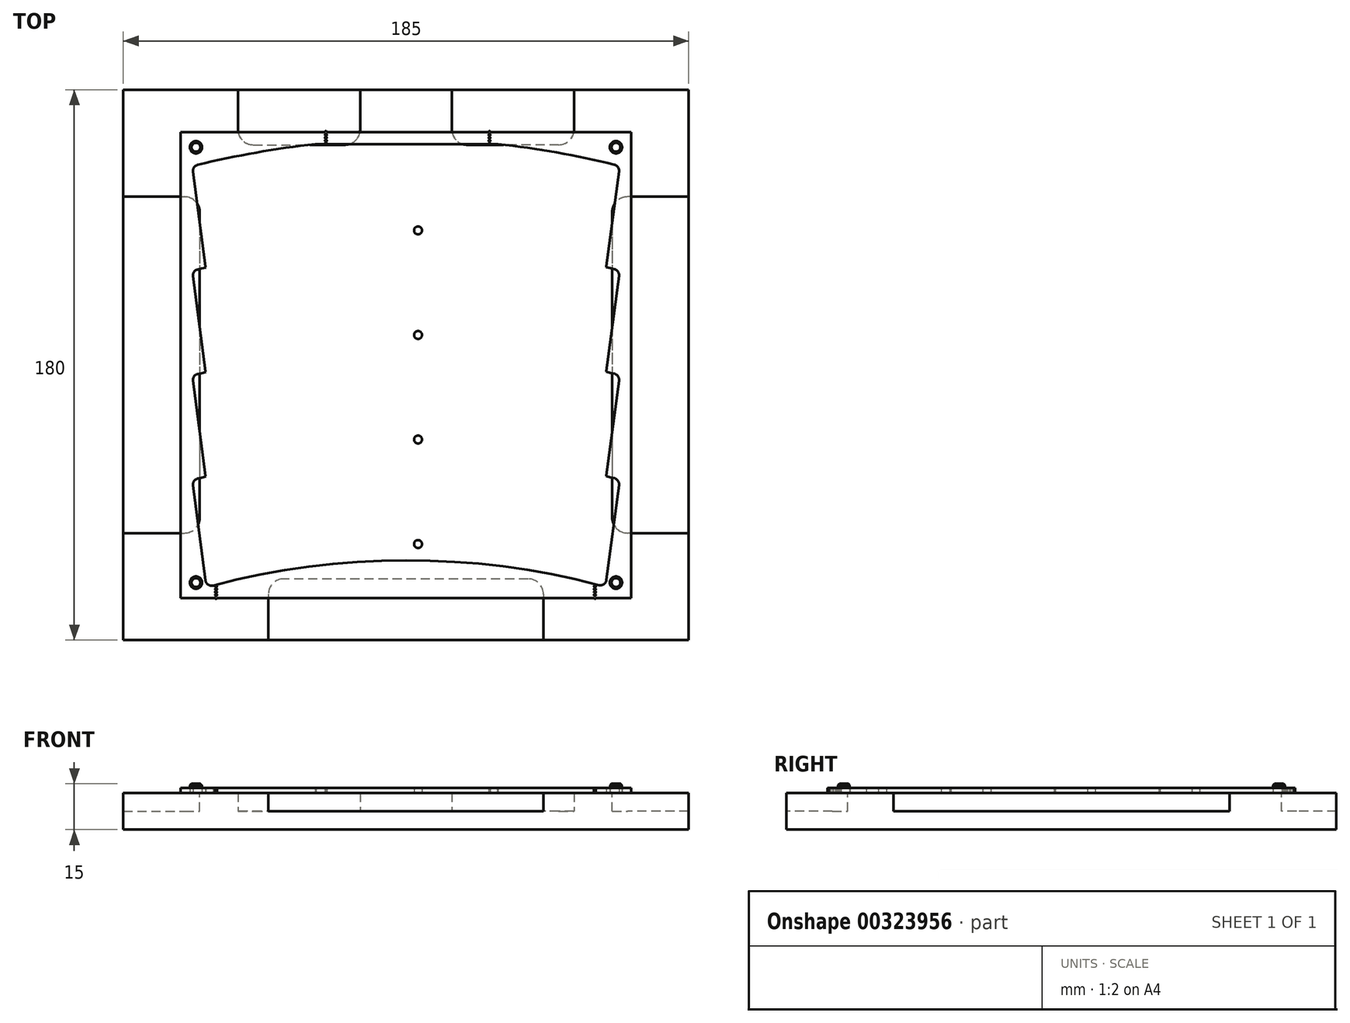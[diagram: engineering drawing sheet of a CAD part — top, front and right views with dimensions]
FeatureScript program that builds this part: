
annotation { "Feature Type Name" : "Feature", "Feature Type Description" : "" }
export const myFeature = defineFeature(function(context is Context, id is Id, definition is map)
    precondition{}
    {
        {
            var Q0;
            Q0=qCreatedBy(makeId("Top.planeOp"),FACE);
            var sketch = newSketch(context, id + "F0", { "sketchPlane" : qUnion([Q0])});
            skLineSegment(sketch, "E0.bottom", {"start": v(92.5, 90) * mm, "end": v(-92.5, 90) * mm});
            skLineSegment(sketch, "E0.top", {"start": v(92.5, -90) * mm, "end": v(-92.5, -90) * mm});
            skLineSegment(sketch, "E0.left", {"start": v(92.5, 90) * mm, "end": v(92.5, -90) * mm});
            skLineSegment(sketch, "E0.right", {"start": v(-92.5, 90) * mm, "end": v(-92.5, -90) * mm});
            skPoint(sketch, "E0.middle", {"position": v(0, 0) * mm});
            skSolve(sketch);
        }
        {
            var Q0;
            Q0 = qSketchRegion(id + "F0", true);
            extrude(context, id + "F1", {"entities" : qUnion([Q0]), "depth" : 12 * mm});
        }
        {
            var Q0;
            Q0=makeQuery(id+"F1.opExtrude","CAP_FACE",FACE,{"disambiguationData":[OSD([sQuery(id+"F0.wireOp",EDGE,"E0.bottom"),sQuery(id+"F0.wireOp",EDGE,"E0.top"),sQuery(id+"F0.wireOp",EDGE,"E0.left"),sQuery(id+"F0.wireOp",EDGE,"E0.right")])],"isStart":false});
            var sketch = newSketch(context, id + "F2", { "sketchPlane" : qUnion([Q0])});
            skLineSegment(sketch, "E1.bottom", {"start": v(117.5, 55) * mm, "end": v(72.5, 55) * mm});
            skLineSegment(sketch, "E1.top", {"start": v(117.5, -55) * mm, "end": v(72.5, -55) * mm});
            skLineSegment(sketch, "E1.left", {"start": v(117.5, 55) * mm, "end": v(117.5, -55) * mm});
            skLineSegment(sketch, "E1.right", {"start": v(67.5, 50) * mm, "end": v(67.5, -50) * mm});
            skPoint(sketch, "E1.middle", {"position": v(92.5, 0) * mm});
            skLineSegment(sketch, "E2.bottom", {"start": v(40, -70) * mm, "end": v(-40, -70) * mm});
            skLineSegment(sketch, "E2.top", {"start": v(45, -110) * mm, "end": v(-45, -110) * mm});
            skLineSegment(sketch, "E2.left", {"start": v(45, -75) * mm, "end": v(45, -110) * mm});
            skLineSegment(sketch, "E2.right", {"start": v(-45, -75) * mm, "end": v(-45, -110) * mm});
            skPoint(sketch, "E2.middle", {"position": v(0, -90) * mm});
            skLineSegment(sketch, "E3.bottom", {"start": v(55, 108) * mm, "end": v(15, 108) * mm});
            skLineSegment(sketch, "E3.top", {"start": v(50, 72) * mm, "end": v(20, 72) * mm});
            skLineSegment(sketch, "E3.left", {"start": v(55, 108) * mm, "end": v(55, 77) * mm});
            skLineSegment(sketch, "E3.right", {"start": v(15, 108) * mm, "end": v(15, 77) * mm});
            skPoint(sketch, "E3.middle", {"position": v(35, 90) * mm});
            skLineSegment(sketch, "E4", {"start": v(0, 90) * mm, "end": v(0, 132.09) * mm});
            skPoint(sketch, "E4.endSnap0", {"position": v(0, 90) * mm});
            skLineSegment(sketch, "E5.MirrorCS", {"start": v(-55, 108) * mm, "end": v(-15, 108) * mm});
            skLineSegment(sketch, "E6.MirrorCS", {"start": v(-50, 72) * mm, "end": v(-20, 72) * mm});
            skLineSegment(sketch, "E7.MirrorCS", {"start": v(-15, 108) * mm, "end": v(-15, 77) * mm});
            skLineSegment(sketch, "E8.MirrorCS", {"start": v(-55, 108) * mm, "end": v(-55, 77) * mm});
            skPoint(sketch, "E9.MirrorP", {"position": v(-35, 90) * mm});
            skPoint(sketch, "E10.visualSharp", {"position": v(55, 72) * mm});
            skArc(sketch, "E10.filletArc", {"start": v(50, 72) * mm, "mid": v(53.54, 73.46) * mm, "end": v(55, 77) * mm});
            skPoint(sketch, "E11.visualSharp", {"position": v(15, 72) * mm});
            skArc(sketch, "E11.filletArc", {"start": v(15, 77) * mm, "mid": v(16.46, 73.46) * mm, "end": v(20, 72) * mm});
            skPoint(sketch, "E12.visualSharp", {"position": v(-15, 72) * mm});
            skArc(sketch, "E12.filletArc", {"start": v(-20, 72) * mm, "mid": v(-16.46, 73.46) * mm, "end": v(-15, 77) * mm});
            skPoint(sketch, "E13.visualSharp", {"position": v(-55, 72) * mm});
            skArc(sketch, "E13.filletArc", {"start": v(-55, 77) * mm, "mid": v(-53.54, 73.46) * mm, "end": v(-50, 72) * mm});
            skPoint(sketch, "E14.visualSharp", {"position": v(67.5, 55) * mm});
            skArc(sketch, "E14.filletArc", {"start": v(72.5, 55) * mm, "mid": v(68.96, 53.54) * mm, "end": v(67.5, 50) * mm});
            skPoint(sketch, "E15.visualSharp", {"position": v(67.5, -55) * mm});
            skArc(sketch, "E15.filletArc", {"start": v(67.5, -50) * mm, "mid": v(68.96, -53.54) * mm, "end": v(72.5, -55) * mm});
            skPoint(sketch, "E16.visualSharp", {"position": v(45, -70) * mm});
            skArc(sketch, "E16.filletArc", {"start": v(45, -75) * mm, "mid": v(43.54, -71.46) * mm, "end": v(40, -70) * mm});
            skPoint(sketch, "E17.visualSharp", {"position": v(-45, -70) * mm});
            skArc(sketch, "E17.filletArc", {"start": v(-40, -70) * mm, "mid": v(-43.54, -71.46) * mm, "end": v(-45, -75) * mm});
            skArc(sketch, "E18.MirrorCS", {"start": v(-72.5, 55) * mm, "mid": v(-68.96, 53.54) * mm, "end": v(-67.5, 50) * mm});
            skArc(sketch, "E19.MirrorCS", {"start": v(-67.5, -50) * mm, "mid": v(-68.96, -53.54) * mm, "end": v(-72.5, -55) * mm});
            skPoint(sketch, "E20.MirrorP", {"position": v(-92.5, 0) * mm});
            skLineSegment(sketch, "E21.MirrorCS", {"start": v(-117.5, 55) * mm, "end": v(-72.5, 55) * mm});
            skLineSegment(sketch, "E22.MirrorCS", {"start": v(-117.5, -55) * mm, "end": v(-72.5, -55) * mm});
            skLineSegment(sketch, "E23.MirrorCS", {"start": v(-67.5, 50) * mm, "end": v(-67.5, -50) * mm});
            skLineSegment(sketch, "E24.MirrorCS", {"start": v(-117.5, 55) * mm, "end": v(-117.5, -55) * mm});
            skPoint(sketch, "E25.MirrorP", {"position": v(-67.5, 55) * mm});
            skPoint(sketch, "E26.MirrorP", {"position": v(-67.5, -55) * mm});
            skSolve(sketch);
        }
        {
            var Q0;
            Q0 = qSketchRegion(id + "F2", true);
            extrude(context, id + "F3", {"entities" : qUnion([Q0]), "operationType" : NewBodyOperationType.REMOVE, "oppositeDirection" : true, "depth" : 6 * mm});
        }
        {
            var Q0;
            Q0=makeQuery(id+"F1.opExtrude","CAP_FACE",FACE,{"disambiguationData":[OSD([sQuery(id+"F0.wireOp",EDGE,"E0.bottom"),sQuery(id+"F0.wireOp",EDGE,"E0.top"),sQuery(id+"F0.wireOp",EDGE,"E0.left"),sQuery(id+"F0.wireOp",EDGE,"E0.right")])],"isStart":false});
            var sketch = newSketch(context, id + "F4", { "sketchPlane" : qUnion([Q0])});
            skCircle(sketch, "E27", {"center": v(-65.48, -53.9) * mm, "radius": 0.3 * mm});
            skCircle(sketch, "E28", {"center": v(-65.36, -54.83) * mm, "radius": 0.3 * mm});
            skCircle(sketch, "E29", {"center": v(-65.23, -55.78) * mm, "radius": 0.3 * mm});
            skCircle(sketch, "E30", {"center": v(-65.6, -52.95) * mm, "radius": 0.3 * mm});
            skCircle(sketch, "E31", {"center": v(-65.1, -56.72) * mm, "radius": 0.3 * mm});
            skCircle(sketch, "E32", {"center": v(-65.73, -52) * mm, "radius": 0.3 * mm});
            skCircle(sketch, "E33", {"center": v(-64.98, -57.66) * mm, "radius": 0.3 * mm});
            skCircle(sketch, "E34", {"center": v(65.22, -55.78) * mm, "radius": 0.3 * mm});
            skCircle(sketch, "E35", {"center": v(65.34, -54.83) * mm, "radius": 0.3 * mm});
            skCircle(sketch, "E36", {"center": v(65.47, -53.9) * mm, "radius": 0.3 * mm});
            skCircle(sketch, "E37", {"center": v(65.1, -56.72) * mm, "radius": 0.3 * mm});
            skCircle(sketch, "E38", {"center": v(65.59, -52.95) * mm, "radius": 0.3 * mm});
            skCircle(sketch, "E39", {"center": v(64.97, -57.66) * mm, "radius": 0.3 * mm});
            skCircle(sketch, "E40", {"center": v(65.71, -52) * mm, "radius": 0.3 * mm});
            skCircle(sketch, "E41", {"center": v(-62.15, -72.4) * mm, "radius": 0.3 * mm});
            skCircle(sketch, "E42", {"center": v(-62.15, -73.35) * mm, "radius": 0.3 * mm});
            skCircle(sketch, "E43", {"center": v(-62.15, -74.3) * mm, "radius": 0.3 * mm});
            skCircle(sketch, "E44", {"center": v(-62.15, -75.25) * mm, "radius": 0.3 * mm});
            skCircle(sketch, "E45", {"center": v(-62.15, -76.2) * mm, "radius": 0.3 * mm});
            skCircle(sketch, "E46", {"center": v(61.85, -72.4) * mm, "radius": 0.3 * mm});
            skCircle(sketch, "E47", {"center": v(61.85, -73.35) * mm, "radius": 0.3 * mm});
            skCircle(sketch, "E48", {"center": v(61.85, -74.3) * mm, "radius": 0.3 * mm});
            skCircle(sketch, "E49", {"center": v(61.85, -75.25) * mm, "radius": 0.3 * mm});
            skCircle(sketch, "E50", {"center": v(61.85, -76.2) * mm, "radius": 0.3 * mm});
            skCircle(sketch, "E51", {"center": v(-26.22, 74.3) * mm, "radius": 0.3 * mm});
            skCircle(sketch, "E52", {"center": v(-26.22, 73.35) * mm, "radius": 0.3 * mm});
            skCircle(sketch, "E53", {"center": v(-26.22, 72.4) * mm, "radius": 0.3 * mm});
            skCircle(sketch, "E54", {"center": v(-26.22, 75.25) * mm, "radius": 0.3 * mm});
            skCircle(sketch, "E55", {"center": v(-26.22, 76.2) * mm, "radius": 0.3 * mm});
            skCircle(sketch, "E56", {"center": v(27.33, 74.3) * mm, "radius": 0.3 * mm});
            skCircle(sketch, "E57", {"center": v(27.33, 73.35) * mm, "radius": 0.3 * mm});
            skCircle(sketch, "E58", {"center": v(27.33, 72.4) * mm, "radius": 0.3 * mm});
            skCircle(sketch, "E59", {"center": v(27.33, 75.25) * mm, "radius": 0.3 * mm});
            skCircle(sketch, "E60", {"center": v(27.33, 76.2) * mm, "radius": 0.3 * mm});
            skCircle(sketch, "E61", {"center": v(-65.48, -19.7) * mm, "radius": 0.3 * mm});
            skCircle(sketch, "E62", {"center": v(-65.36, -20.63) * mm, "radius": 0.3 * mm});
            skCircle(sketch, "E63", {"center": v(-65.23, -21.58) * mm, "radius": 0.3 * mm});
            skCircle(sketch, "E64", {"center": v(-65.6, -18.75) * mm, "radius": 0.3 * mm});
            skCircle(sketch, "E65", {"center": v(-65.1, -22.52) * mm, "radius": 0.3 * mm});
            skCircle(sketch, "E66", {"center": v(-65.73, -17.8) * mm, "radius": 0.3 * mm});
            skCircle(sketch, "E67", {"center": v(-64.98, -23.46) * mm, "radius": 0.3 * mm});
            skCircle(sketch, "E68", {"center": v(65.22, -21.58) * mm, "radius": 0.3 * mm});
            skCircle(sketch, "E69", {"center": v(65.34, -20.63) * mm, "radius": 0.3 * mm});
            skCircle(sketch, "E70", {"center": v(65.47, -19.7) * mm, "radius": 0.3 * mm});
            skCircle(sketch, "E71", {"center": v(65.1, -22.52) * mm, "radius": 0.3 * mm});
            skCircle(sketch, "E72", {"center": v(65.59, -18.75) * mm, "radius": 0.3 * mm});
            skCircle(sketch, "E73", {"center": v(64.97, -23.46) * mm, "radius": 0.3 * mm});
            skCircle(sketch, "E74", {"center": v(65.71, -17.8) * mm, "radius": 0.3 * mm});
            skCircle(sketch, "E75", {"center": v(-65.48, 14.5) * mm, "radius": 0.3 * mm});
            skCircle(sketch, "E76", {"center": v(-65.36, 13.57) * mm, "radius": 0.3 * mm});
            skCircle(sketch, "E77", {"center": v(-65.23, 12.62) * mm, "radius": 0.3 * mm});
            skCircle(sketch, "E78", {"center": v(-65.6, 15.45) * mm, "radius": 0.3 * mm});
            skCircle(sketch, "E79", {"center": v(-65.1, 11.68) * mm, "radius": 0.3 * mm});
            skCircle(sketch, "E80", {"center": v(-65.73, 16.4) * mm, "radius": 0.3 * mm});
            skCircle(sketch, "E81", {"center": v(-64.98, 10.74) * mm, "radius": 0.3 * mm});
            skCircle(sketch, "E82", {"center": v(65.22, 12.62) * mm, "radius": 0.3 * mm});
            skCircle(sketch, "E83", {"center": v(65.34, 13.57) * mm, "radius": 0.3 * mm});
            skCircle(sketch, "E84", {"center": v(65.47, 14.5) * mm, "radius": 0.3 * mm});
            skCircle(sketch, "E85", {"center": v(65.1, 11.68) * mm, "radius": 0.3 * mm});
            skCircle(sketch, "E86", {"center": v(65.59, 15.45) * mm, "radius": 0.3 * mm});
            skCircle(sketch, "E87", {"center": v(64.97, 10.74) * mm, "radius": 0.3 * mm});
            skCircle(sketch, "E88", {"center": v(65.71, 16.4) * mm, "radius": 0.3 * mm});
            skCircle(sketch, "E89", {"center": v(-65.48, 48.7) * mm, "radius": 0.3 * mm});
            skCircle(sketch, "E90", {"center": v(-65.36, 47.77) * mm, "radius": 0.3 * mm});
            skCircle(sketch, "E91", {"center": v(-65.23, 46.82) * mm, "radius": 0.3 * mm});
            skCircle(sketch, "E92", {"center": v(-65.6, 49.65) * mm, "radius": 0.3 * mm});
            skCircle(sketch, "E93", {"center": v(-65.1, 45.88) * mm, "radius": 0.3 * mm});
            skCircle(sketch, "E94", {"center": v(-65.73, 50.6) * mm, "radius": 0.3 * mm});
            skCircle(sketch, "E95", {"center": v(-64.98, 44.94) * mm, "radius": 0.3 * mm});
            skCircle(sketch, "E96", {"center": v(65.22, 46.82) * mm, "radius": 0.3 * mm});
            skCircle(sketch, "E97", {"center": v(65.34, 47.77) * mm, "radius": 0.3 * mm});
            skCircle(sketch, "E98", {"center": v(65.47, 48.7) * mm, "radius": 0.3 * mm});
            skCircle(sketch, "E99", {"center": v(65.1, 45.88) * mm, "radius": 0.3 * mm});
            skCircle(sketch, "E100", {"center": v(65.59, 49.65) * mm, "radius": 0.3 * mm});
            skCircle(sketch, "E101", {"center": v(64.97, 44.94) * mm, "radius": 0.3 * mm});
            skCircle(sketch, "E102", {"center": v(65.71, 50.6) * mm, "radius": 0.3 * mm});
            skCircle(sketch, "E103", {"center": v(-67.04, -52.03) * mm, "radius": 0.9 * mm});
            skCircle(sketch, "E104", {"center": v(-66.25, -57.98) * mm, "radius": 0.9 * mm});
            skCircle(sketch, "E105", {"center": v(66.24, -57.98) * mm, "radius": 0.9 * mm});
            skCircle(sketch, "E106", {"center": v(67.02, -52.03) * mm, "radius": 0.9 * mm});
            skCircle(sketch, "E107", {"center": v(-67.04, -17.83) * mm, "radius": 0.9 * mm});
            skCircle(sketch, "E108", {"center": v(-66.25, -23.78) * mm, "radius": 0.9 * mm});
            skCircle(sketch, "E109", {"center": v(66.24, -23.78) * mm, "radius": 0.9 * mm});
            skCircle(sketch, "E110", {"center": v(67.02, -17.83) * mm, "radius": 0.9 * mm});
            skCircle(sketch, "E111", {"center": v(-67.04, 16.37) * mm, "radius": 0.9 * mm});
            skCircle(sketch, "E112", {"center": v(-66.25, 10.42) * mm, "radius": 0.9 * mm});
            skCircle(sketch, "E113", {"center": v(66.24, 10.42) * mm, "radius": 0.9 * mm});
            skCircle(sketch, "E114", {"center": v(67.02, 16.37) * mm, "radius": 0.9 * mm});
            skCircle(sketch, "E115", {"center": v(-67.04, 50.57) * mm, "radius": 0.9 * mm});
            skCircle(sketch, "E116", {"center": v(-66.25, 44.62) * mm, "radius": 0.9 * mm});
            skCircle(sketch, "E117", {"center": v(66.24, 44.62) * mm, "radius": 0.9 * mm});
            skCircle(sketch, "E118", {"center": v(67.02, 50.57) * mm, "radius": 0.9 * mm});
            skCircle(sketch, "E119", {"center": v(3.96, 44) * mm, "radius": 1.3 * mm});
            skCircle(sketch, "E120", {"center": v(-3.94, 44) * mm, "radius": 1.3 * mm});
            skCircle(sketch, "E121", {"center": v(3.96, 9.8) * mm, "radius": 1.3 * mm});
            skCircle(sketch, "E122", {"center": v(-3.94, 9.8) * mm, "radius": 1.3 * mm});
            skCircle(sketch, "E123", {"center": v(3.96, -24.4) * mm, "radius": 1.3 * mm});
            skCircle(sketch, "E124", {"center": v(-3.94, -24.4) * mm, "radius": 1.3 * mm});
            skCircle(sketch, "E125", {"center": v(3.96, -58.6) * mm, "radius": 1.3 * mm});
            skCircle(sketch, "E126", {"center": v(-3.94, -58.6) * mm, "radius": 1.3 * mm});
            skCircle(sketch, "E127", {"center": v(-68.73, -71.2) * mm, "radius": 2 * mm});
            skCircle(sketch, "E128", {"center": v(-68.73, 71.2) * mm, "radius": 2 * mm});
            skCircle(sketch, "E129", {"center": v(68.73, -71.2) * mm, "radius": 2 * mm});
            skCircle(sketch, "E130", {"center": v(68.73, 71.2) * mm, "radius": 2 * mm});
            skLineSegment(sketch, "E131", {"start": v(-73.73, -76.2) * mm, "end": v(-73.73, 76.2) * mm});
            skLineSegment(sketch, "E132", {"start": v(-73.73, 76.2) * mm, "end": v(73.73, 76.2) * mm});
            skLineSegment(sketch, "E133", {"start": v(73.73, 76.2) * mm, "end": v(73.73, -76.2) * mm});
            skLineSegment(sketch, "E134", {"start": v(73.73, -76.2) * mm, "end": v(-73.73, -76.2) * mm});
            skArc(sketch, "E135", {"start": v(66.03, 50.7) * mm, "mid": v(66.9, 49.58) * mm, "end": v(68.01, 50.44) * mm});
            skArc(sketch, "E136", {"start": v(67.23, 44.5) * mm, "mid": v(66.37, 45.61) * mm, "end": v(65.25, 44.75) * mm});
            skArc(sketch, "E137", {"start": v(66.03, 16.5) * mm, "mid": v(66.9, 15.38) * mm, "end": v(68.01, 16.24) * mm});
            skArc(sketch, "E138", {"start": v(67.23, 10.3) * mm, "mid": v(66.37, 11.41) * mm, "end": v(65.25, 10.55) * mm});
            skArc(sketch, "E139", {"start": v(66.03, -17.7) * mm, "mid": v(66.9, -18.82) * mm, "end": v(68.01, -17.96) * mm});
            skArc(sketch, "E140", {"start": v(67.23, -23.9) * mm, "mid": v(66.37, -22.79) * mm, "end": v(65.25, -23.65) * mm});
            skArc(sketch, "E141", {"start": v(66.03, -51.9) * mm, "mid": v(66.9, -53.02) * mm, "end": v(68.01, -52.16) * mm});
            skArc(sketch, "E142", {"start": v(67.23, -58.1) * mm, "mid": v(66.37, -56.99) * mm, "end": v(65.25, -57.85) * mm});
            skArc(sketch, "E143", {"start": v(-65.26, -57.85) * mm, "mid": v(-66.38, -56.99) * mm, "end": v(-67.25, -58.1) * mm});
            skArc(sketch, "E144", {"start": v(-68.03, -52.16) * mm, "mid": v(-66.9, -53.02) * mm, "end": v(-66.04, -51.9) * mm});
            skArc(sketch, "E145", {"start": v(-65.26, -23.65) * mm, "mid": v(-66.38, -22.79) * mm, "end": v(-67.25, -23.9) * mm});
            skArc(sketch, "E146", {"start": v(-68.03, -17.96) * mm, "mid": v(-66.9, -18.82) * mm, "end": v(-66.04, -17.7) * mm});
            skArc(sketch, "E147", {"start": v(-65.26, 10.55) * mm, "mid": v(-66.38, 11.41) * mm, "end": v(-67.25, 10.3) * mm});
            skArc(sketch, "E148", {"start": v(-68.03, 16.24) * mm, "mid": v(-66.9, 15.38) * mm, "end": v(-66.04, 16.5) * mm});
            skArc(sketch, "E149", {"start": v(-65.26, 44.75) * mm, "mid": v(-66.38, 45.61) * mm, "end": v(-67.25, 44.5) * mm});
            skArc(sketch, "E150", {"start": v(-68.03, 50.44) * mm, "mid": v(-66.9, 49.58) * mm, "end": v(-66.04, 50.7) * mm});
            skLineSegment(sketch, "E151", {"start": v(-63.64, 32.4) * mm, "end": v(-67.73, 63.47) * mm});
            skArc(sketch, "E152", {"start": v(-29.45, 70.2) * mm, "mid": v(-48.7, 67.5) * mm, "end": v(-67.73, 63.47) * mm});
            skLineSegment(sketch, "E153", {"start": v(-29.45, 70.2) * mm, "end": v(29.92, 70.2) * mm});
            skArc(sketch, "E154", {"start": v(67.73, 63.58) * mm, "mid": v(48.94, 67.53) * mm, "end": v(29.92, 70.2) * mm});
            skLineSegment(sketch, "E155", {"start": v(67.73, 63.58) * mm, "end": v(63.64, 32.52) * mm});
            skLineSegment(sketch, "E156", {"start": v(63.64, 32.52) * mm, "end": v(63.64, 32.52) * mm});
            skArc(sketch, "E157", {"start": v(63.64, 32.52) * mm, "mid": v(0, 40.7) * mm, "end": v(-63.64, 32.4) * mm});
            skLineSegment(sketch, "E158", {"start": v(-63.64, -1.8) * mm, "end": v(-67.73, 29.27) * mm});
            skArc(sketch, "E159", {"start": v(-29.45, 36) * mm, "mid": v(-48.7, 33.3) * mm, "end": v(-67.73, 29.27) * mm});
            skLineSegment(sketch, "E160", {"start": v(-29.45, 36) * mm, "end": v(29.92, 36) * mm});
            skArc(sketch, "E161", {"start": v(67.73, 29.38) * mm, "mid": v(48.94, 33.33) * mm, "end": v(29.92, 36) * mm});
            skLineSegment(sketch, "E162", {"start": v(67.73, 29.38) * mm, "end": v(63.64, -1.68) * mm});
            skLineSegment(sketch, "E163", {"start": v(63.64, -1.68) * mm, "end": v(63.64, -1.68) * mm});
            skArc(sketch, "E164", {"start": v(63.64, -1.68) * mm, "mid": v(0, 6.5) * mm, "end": v(-63.64, -1.8) * mm});
            skLineSegment(sketch, "E165", {"start": v(-63.64, -36) * mm, "end": v(-67.73, -4.93) * mm});
            skArc(sketch, "E166", {"start": v(-29.45, 1.8) * mm, "mid": v(-48.7, -0.9) * mm, "end": v(-67.73, -4.93) * mm});
            skLineSegment(sketch, "E167", {"start": v(-29.45, 1.8) * mm, "end": v(29.92, 1.8) * mm});
            skArc(sketch, "E168", {"start": v(67.73, -4.82) * mm, "mid": v(48.94, -0.87) * mm, "end": v(29.92, 1.8) * mm});
            skLineSegment(sketch, "E169", {"start": v(67.73, -4.82) * mm, "end": v(63.64, -35.88) * mm});
            skLineSegment(sketch, "E170", {"start": v(63.64, -35.88) * mm, "end": v(63.64, -35.88) * mm});
            skArc(sketch, "E171", {"start": v(63.64, -35.88) * mm, "mid": v(0, -27.7) * mm, "end": v(-63.64, -36) * mm});
            skLineSegment(sketch, "E172", {"start": v(-63.64, -70.2) * mm, "end": v(-67.73, -39.13) * mm});
            skArc(sketch, "E173", {"start": v(-29.45, -32.4) * mm, "mid": v(-48.7, -35.1) * mm, "end": v(-67.73, -39.13) * mm});
            skLineSegment(sketch, "E174", {"start": v(-29.45, -32.4) * mm, "end": v(29.92, -32.4) * mm});
            skArc(sketch, "E175", {"start": v(67.73, -39.02) * mm, "mid": v(48.94, -35.07) * mm, "end": v(29.92, -32.4) * mm});
            skLineSegment(sketch, "E176", {"start": v(67.73, -39.02) * mm, "end": v(63.64, -70.08) * mm});
            skLineSegment(sketch, "E177", {"start": v(63.64, -70.08) * mm, "end": v(63.64, -70.08) * mm});
            skArc(sketch, "E178", {"start": v(63.64, -70.08) * mm, "mid": v(0, -61.9) * mm, "end": v(-63.64, -70.2) * mm});
            skArc(sketch, "E179", {"start": v(-65.62, -70.45) * mm, "mid": v(-64.75, -71.86) * mm, "end": v(-63.12, -72.13) * mm});
            skLineSegment(sketch, "E180", {"start": v(-65.62, -70.45) * mm, "end": v(-69.7, -39.4) * mm});
            skArc(sketch, "E181", {"start": v(-68.2, -37.2) * mm, "mid": v(-69.38, -38) * mm, "end": v(-69.7, -39.4) * mm});
            skLineSegment(sketch, "E182", {"start": v(-68.2, -37.2) * mm, "end": v(-66.88, -36.87) * mm});
            skLineSegment(sketch, "E183", {"start": v(-66.88, -36.87) * mm, "end": v(-65.56, -36.55) * mm});
            skLineSegment(sketch, "E184", {"start": v(-65.56, -36.55) * mm, "end": v(-65.6, -36.4) * mm});
            skLineSegment(sketch, "E185", {"start": v(-65.6, -36.4) * mm, "end": v(-65.62, -36.25) * mm});
            skLineSegment(sketch, "E186", {"start": v(-65.62, -36.25) * mm, "end": v(-69.7, -5.2) * mm});
            skArc(sketch, "E187", {"start": v(-68.2, -2.99) * mm, "mid": v(-69.38, -3.8) * mm, "end": v(-69.7, -5.2) * mm});
            skLineSegment(sketch, "E188", {"start": v(-68.2, -2.99) * mm, "end": v(-66.88, -2.67) * mm});
            skLineSegment(sketch, "E189", {"start": v(-66.88, -2.67) * mm, "end": v(-65.56, -2.35) * mm});
            skLineSegment(sketch, "E190", {"start": v(-65.56, -2.35) * mm, "end": v(-65.6, -2.2) * mm});
            skLineSegment(sketch, "E191", {"start": v(-65.6, -2.2) * mm, "end": v(-65.62, -2.05) * mm});
            skLineSegment(sketch, "E192", {"start": v(-65.62, -2.05) * mm, "end": v(-69.7, 29) * mm});
            skArc(sketch, "E193", {"start": v(-68.2, 31.21) * mm, "mid": v(-69.38, 30.4) * mm, "end": v(-69.7, 29) * mm});
            skLineSegment(sketch, "E194", {"start": v(-68.2, 31.21) * mm, "end": v(-66.88, 31.53) * mm});
            skLineSegment(sketch, "E195", {"start": v(-66.88, 31.53) * mm, "end": v(-65.56, 31.85) * mm});
            skLineSegment(sketch, "E196", {"start": v(-65.56, 31.85) * mm, "end": v(-65.6, 32) * mm});
            skLineSegment(sketch, "E197", {"start": v(-65.6, 32) * mm, "end": v(-65.62, 32.15) * mm});
            skLineSegment(sketch, "E198", {"start": v(-65.62, 32.15) * mm, "end": v(-69.7, 63.2) * mm});
            skArc(sketch, "E199", {"start": v(-68.2, 65.41) * mm, "mid": v(-69.38, 64.6) * mm, "end": v(-69.7, 63.2) * mm});
            skArc(sketch, "E200", {"start": v(-29.66, 72.19) * mm, "mid": v(-49.05, 69.46) * mm, "end": v(-68.2, 65.41) * mm});
            skLineSegment(sketch, "E201", {"start": v(-29.66, 72.19) * mm, "end": v(-29.56, 72.2) * mm});
            skLineSegment(sketch, "E202", {"start": v(-29.56, 72.2) * mm, "end": v(-29.45, 72.2) * mm});
            skLineSegment(sketch, "E203", {"start": v(-29.45, 72.2) * mm, "end": v(29.92, 72.2) * mm});
            skLineSegment(sketch, "E204", {"start": v(29.92, 72.2) * mm, "end": v(29.93, 72.2) * mm});
            skLineSegment(sketch, "E205", {"start": v(29.93, 72.2) * mm, "end": v(29.92, 72.2) * mm});
            skLineSegment(sketch, "E206", {"start": v(29.92, 72.2) * mm, "end": v(30.03, 72.2) * mm});
            skLineSegment(sketch, "E207", {"start": v(30.03, 72.2) * mm, "end": v(30.14, 72.19) * mm});
            skArc(sketch, "E208", {"start": v(68.2, 65.53) * mm, "mid": v(49.28, 69.5) * mm, "end": v(30.14, 72.19) * mm});
            skArc(sketch, "E209", {"start": v(69.7, 63.32) * mm, "mid": v(69.38, 64.71) * mm, "end": v(68.2, 65.53) * mm});
            skLineSegment(sketch, "E210", {"start": v(69.7, 63.32) * mm, "end": v(65.62, 32.26) * mm});
            skLineSegment(sketch, "E211", {"start": v(65.62, 32.26) * mm, "end": v(65.6, 32.11) * mm});
            skLineSegment(sketch, "E212", {"start": v(65.6, 32.11) * mm, "end": v(65.56, 31.96) * mm});
            skLineSegment(sketch, "E213", {"start": v(65.56, 31.96) * mm, "end": v(66.88, 31.65) * mm});
            skLineSegment(sketch, "E214", {"start": v(66.88, 31.65) * mm, "end": v(68.2, 31.33) * mm});
            skArc(sketch, "E215", {"start": v(69.7, 29.12) * mm, "mid": v(69.38, 30.51) * mm, "end": v(68.2, 31.33) * mm});
            skLineSegment(sketch, "E216", {"start": v(69.7, 29.12) * mm, "end": v(65.62, -1.94) * mm});
            skLineSegment(sketch, "E217", {"start": v(65.62, -1.94) * mm, "end": v(65.6, -2.09) * mm});
            skLineSegment(sketch, "E218", {"start": v(65.6, -2.09) * mm, "end": v(65.56, -2.24) * mm});
            skLineSegment(sketch, "E219", {"start": v(65.56, -2.24) * mm, "end": v(66.88, -2.55) * mm});
            skLineSegment(sketch, "E220", {"start": v(66.88, -2.55) * mm, "end": v(68.2, -2.87) * mm});
            skArc(sketch, "E221", {"start": v(69.7, -5.08) * mm, "mid": v(69.38, -3.69) * mm, "end": v(68.2, -2.87) * mm});
            skLineSegment(sketch, "E222", {"start": v(69.7, -5.08) * mm, "end": v(65.62, -36.14) * mm});
            skLineSegment(sketch, "E223", {"start": v(65.62, -36.14) * mm, "end": v(65.6, -36.29) * mm});
            skLineSegment(sketch, "E224", {"start": v(65.6, -36.29) * mm, "end": v(65.56, -36.44) * mm});
            skLineSegment(sketch, "E225", {"start": v(65.56, -36.44) * mm, "end": v(66.88, -36.75) * mm});
            skLineSegment(sketch, "E226", {"start": v(66.88, -36.75) * mm, "end": v(68.2, -37.07) * mm});
            skArc(sketch, "E227", {"start": v(69.7, -39.28) * mm, "mid": v(69.38, -37.89) * mm, "end": v(68.2, -37.07) * mm});
            skLineSegment(sketch, "E228", {"start": v(69.7, -39.28) * mm, "end": v(69.7, -39.28) * mm});
            skLineSegment(sketch, "E229", {"start": v(69.7, -39.28) * mm, "end": v(65.62, -70.34) * mm});
            skArc(sketch, "E230", {"start": v(63.13, -72.01) * mm, "mid": v(64.75, -71.74) * mm, "end": v(65.62, -70.34) * mm});
            skArc(sketch, "E231", {"start": v(63.13, -72.01) * mm, "mid": v(0, -63.9) * mm, "end": v(-63.12, -72.13) * mm});
            skLineSegment(sketch, "E232", {"start": v(-63.12, -72.13) * mm, "end": v(-63.12, -72.13) * mm});
            skSolve(sketch);
        }
        {
            var Q0;
            Q0 = qSketchRegion(id + "F4", true);
            var Q1;
            Q1=makeQuery(id+"F4.imprint","IMPRINT",FACE,{"disambiguationData":[TD([[makeQuery(id+"F4.imprint","IMPRINT",EDGE,{"derivedFrom":sQuery(id+"F4.wireOp",EDGE,"E119")}),1.0]])]});
            var Q2;
            Q2=makeQuery(id+"F4.imprint","IMPRINT",FACE,{"disambiguationData":[TD([[makeQuery(id+"F4.imprint","IMPRINT",EDGE,{"derivedFrom":sQuery(id+"F4.wireOp",EDGE,"E121")}),1.0]])]});
            var Q3;
            Q3=makeQuery(id+"F4.imprint","IMPRINT",FACE,{"disambiguationData":[TD([[makeQuery(id+"F4.imprint","IMPRINT",EDGE,{"derivedFrom":sQuery(id+"F4.wireOp",EDGE,"E123")}),1.0]])]});
            var Q4;
            Q4=makeQuery(id+"F4.imprint","IMPRINT",FACE,{"disambiguationData":[TD([[makeQuery(id+"F4.imprint","IMPRINT",EDGE,{"derivedFrom":sQuery(id+"F4.wireOp",EDGE,"E125")}),1.0]])]});
            extrude(context, id + "F5", {"entities" : qUnion([Q0, Q1, Q2, Q3, Q4]), "depth" : 1.6 * mm});
        }
        {
            var Q0;
            Q0=makeQuery(id+"F1.opExtrude","CAP_FACE",FACE,{"disambiguationData":[OSD([sQuery(id+"F0.wireOp",EDGE,"E0.bottom"),sQuery(id+"F0.wireOp",EDGE,"E0.top"),sQuery(id+"F0.wireOp",EDGE,"E0.left"),sQuery(id+"F0.wireOp",EDGE,"E0.right")])],"isStart":false});
            var sketch = newSketch(context, id + "F6", { "sketchPlane" : qUnion([Q0])});
            skLineSegment(sketch, "E233.0.0", {"start": v(-73.73, 76.2) * mm, "end": v(-73.73, -76.2) * mm, "construction": true});
            skLineSegment(sketch, "E233.0.1", {"start": v(-73.73, -76.2) * mm, "end": v(-62.45, -76.2) * mm, "construction": true});
            skArc(sketch, "E233.0.2", {"start": v(-62.45, -76.2) * mm, "mid": v(-62.15, -76.5) * mm, "end": v(-61.85, -76.2) * mm, "construction": true});
            skLineSegment(sketch, "E233.0.3", {"start": v(-61.85, -76.2) * mm, "end": v(61.55, -76.2) * mm, "construction": true});
            skArc(sketch, "E233.0.4", {"start": v(61.55, -76.2) * mm, "mid": v(61.85, -76.5) * mm, "end": v(62.15, -76.2) * mm, "construction": true});
            skLineSegment(sketch, "E233.0.5", {"start": v(62.15, -76.2) * mm, "end": v(73.73, -76.2) * mm, "construction": true});
            skLineSegment(sketch, "E233.0.6", {"start": v(73.73, -76.2) * mm, "end": v(73.73, 76.2) * mm, "construction": true});
            skLineSegment(sketch, "E233.0.7", {"start": v(73.73, 76.2) * mm, "end": v(27.63, 76.2) * mm, "construction": true});
            skArc(sketch, "E233.0.8", {"start": v(27.63, 76.2) * mm, "mid": v(27.33, 76.5) * mm, "end": v(27.03, 76.2) * mm, "construction": true});
            skLineSegment(sketch, "E233.0.9", {"start": v(27.03, 76.2) * mm, "end": v(-25.92, 76.2) * mm, "construction": true});
            skArc(sketch, "E233.0.10", {"start": v(-25.92, 76.2) * mm, "mid": v(-26.22, 76.5) * mm, "end": v(-26.52, 76.2) * mm, "construction": true});
            skLineSegment(sketch, "E233.0.11", {"start": v(-26.52, 76.2) * mm, "end": v(-73.73, 76.2) * mm, "construction": true});
            skCircle(sketch, "E234.0", {"center": v(-68.73, 71.2) * mm, "radius": 2 * mm, "construction": true});
            skCircle(sketch, "E235.0", {"center": v(68.73, 71.2) * mm, "radius": 2 * mm, "construction": true});
            skCircle(sketch, "E236.0", {"center": v(68.73, -71.2) * mm, "radius": 2 * mm, "construction": true});
            skCircle(sketch, "E237.0", {"center": v(-68.73, -71.2) * mm, "radius": 2 * mm, "construction": true});
            skCircle(sketch, "E238", {"center": v(68.73, 71.2) * mm, "radius": 1.95 * mm});
            skCircle(sketch, "E239", {"center": v(-68.73, 71.2) * mm, "radius": 1.95 * mm});
            skCircle(sketch, "E240", {"center": v(68.73, -71.2) * mm, "radius": 1.95 * mm});
            skCircle(sketch, "E241", {"center": v(-68.73, -71.2) * mm, "radius": 1.95 * mm});
            skSolve(sketch);
        }
        {
            var Q0;
            Q0 = qSketchRegion(id + "F6", true);
            extrude(context, id + "F7", {"entities" : qUnion([Q0]), "operationType" : NewBodyOperationType.ADD, "depth" : 3 * mm});
        }
        {
            var Q0;
            Q0=makeQuery(id+"F7.opExtrude","CAP_EDGE",EDGE,{"disambiguationData":[OSD([sQuery(id+"F6.wireOp",EDGE,"E241")])],"isStart":false});
            var Q1;
            Q1=makeQuery(id+"F7.opExtrude","CAP_EDGE",EDGE,{"disambiguationData":[OSD([sQuery(id+"F6.wireOp",EDGE,"E240")])],"isStart":false});
            var Q2;
            Q2=makeQuery(id+"F7.opExtrude","CAP_EDGE",EDGE,{"disambiguationData":[OSD([sQuery(id+"F6.wireOp",EDGE,"E238")])],"isStart":false});
            var Q3;
            Q3=makeQuery(id+"F7.opExtrude","CAP_EDGE",EDGE,{"disambiguationData":[OSD([sQuery(id+"F6.wireOp",EDGE,"E239")])],"isStart":false});
            chamfer(context, id + "F8", {"entities" : qUnion([Q0, Q1, Q2, Q3]), "width" : .5 * mm, "tangentPropagation" : true});
        }
    });
